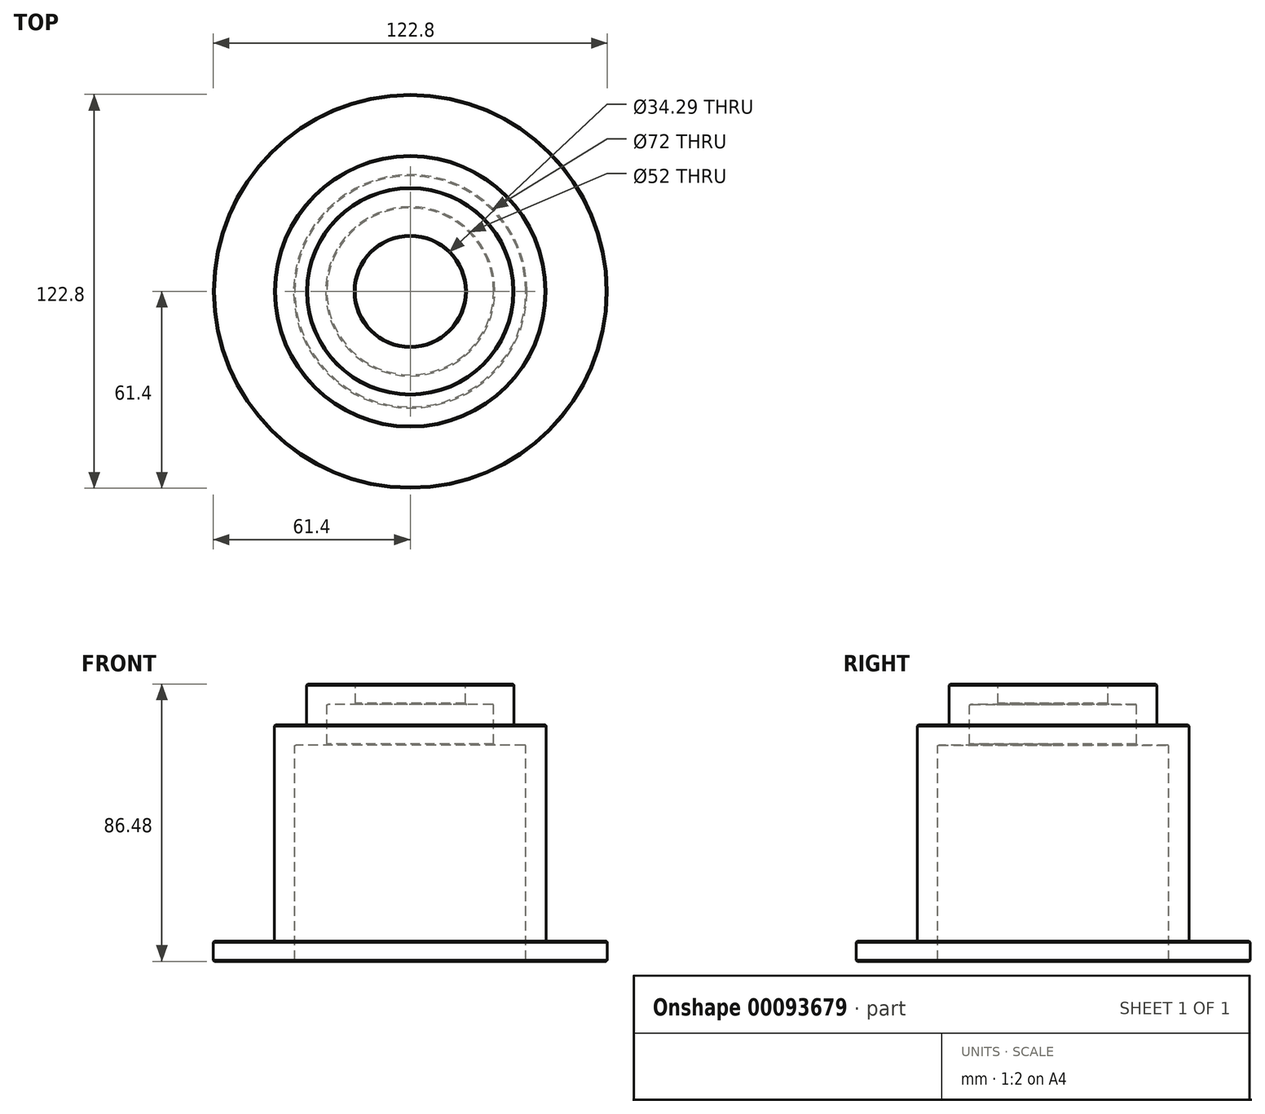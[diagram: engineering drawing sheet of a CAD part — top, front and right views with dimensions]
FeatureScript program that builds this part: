
annotation { "Feature Type Name" : "Feature", "Feature Type Description" : "" }
export const myFeature = defineFeature(function(context is Context, id is Id, definition is map)
    precondition{}
    {
        {
            var Q0;
            Q0=qCreatedBy(makeId("Front.planeOp"),FACE);
            var sketch = newSketch(context, id + "F0", { "sketchPlane" : qUnion([Q0])});
            skLineSegment(sketch, "E0", {"start": v(-17.15, 0) * mm, "end": v(-26, 0) * mm});
            skLineSegment(sketch, "E1", {"start": v(-26, 0) * mm, "end": v(-26, -12.7) * mm});
            skLineSegment(sketch, "E2", {"start": v(-26, -12.7) * mm, "end": v(-36, -12.7) * mm});
            skLineSegment(sketch, "E3", {"start": v(-36, -12.7) * mm, "end": v(-36, -80.13) * mm});
            skLineSegment(sketch, "E4", {"start": v(-36, -80.13) * mm, "end": v(-61.4, -80.13) * mm});
            skLineSegment(sketch, "E5.0", {"start": v(-42.35, -73.78) * mm, "end": v(-61.4, -73.78) * mm});
            skLineSegment(sketch, "E5.1", {"start": v(-17.15, 6.35) * mm, "end": v(-32.35, 6.35) * mm});
            skLineSegment(sketch, "E5.2", {"start": v(-32.35, 6.35) * mm, "end": v(-32.35, -6.35) * mm});
            skLineSegment(sketch, "E5.3", {"start": v(-32.35, -6.35) * mm, "end": v(-42.35, -6.35) * mm});
            skLineSegment(sketch, "E5.4", {"start": v(-42.35, -6.35) * mm, "end": v(-42.35, -73.78) * mm});
            skLineSegment(sketch, "E6", {"start": v(-17.15, 6.35) * mm, "end": v(-17.15, 0) * mm});
            skLineSegment(sketch, "E7", {"start": v(-61.4, -73.78) * mm, "end": v(-61.4, -80.13) * mm});
            skLineSegment(sketch, "E8", {"start": v(0, 32.3) * mm, "end": v(0, -87.06) * mm, "construction": true});
            skSolve(sketch);
        }
        {
            var Q0;
            Q0=qSketchRegion(id+"F0",true);
            var Q1;
            Q1=sQuery(id+"F0.wireOp",EDGE,"E8");
            revolve(context, id + "F1", {"entities" : qUnion([Q0]), "axis" : qUnion([Q1]), "revolveType" : RevolveType.FULL});
        }
        {
            var Q0;
            Q0=makeQuery(id+"F1.opRevolve","SWEPT_EDGE",EDGE,{"disambiguationData":[OSD([sQuery(id+"F0.wireOp",EDGE,"E5.2"),sQuery(id+"F0.wireOp",EDGE,"E5.3")])]});
            var Q1;
            Q1=makeQuery(id+"F1.opRevolve","SWEPT_EDGE",EDGE,{"disambiguationData":[OSD([sQuery(id+"F0.wireOp",EDGE,"E5.0"),sQuery(id+"F0.wireOp",EDGE,"E5.4")])]});
            var Q2;
            Q2=makeQuery(id+"F1.opRevolve","SWEPT_EDGE",EDGE,{"disambiguationData":[OSD([sQuery(id+"F0.wireOp",EDGE,"E2"),sQuery(id+"F0.wireOp",EDGE,"E3")])]});
            var Q3;
            Q3=makeQuery(id+"F1.opRevolve","SWEPT_EDGE",EDGE,{"disambiguationData":[OSD([sQuery(id+"F0.wireOp",EDGE,"E0"),sQuery(id+"F0.wireOp",EDGE,"E1")])]});
            fillet(context, id + "F2", {"entities" : qUnion([Q0, Q1, Q2, Q3]), "radius" : 0.38 * mm, "tangentPropagation" : true, "allowEdgeOverflow" : false});
        }
        {
            var Q0;
            Q0=makeQuery(id+"F1.opRevolve","SWEPT_EDGE",EDGE,{"disambiguationData":[OSD([sQuery(id+"F0.wireOp",EDGE,"E5.1"),sQuery(id+"F0.wireOp",EDGE,"E5.2")])]});
            var Q1;
            Q1=makeQuery(id+"F1.opRevolve","SWEPT_EDGE",EDGE,{"disambiguationData":[OSD([sQuery(id+"F0.wireOp",EDGE,"E5.1"),sQuery(id+"F0.wireOp",EDGE,"E6")])]});
            var Q2;
            Q2=makeQuery(id+"F1.opRevolve","SWEPT_EDGE",EDGE,{"disambiguationData":[OSD([sQuery(id+"F0.wireOp",EDGE,"E5.3"),sQuery(id+"F0.wireOp",EDGE,"E5.4")])]});
            var Q3;
            Q3=makeQuery(id+"F1.opRevolve","SWEPT_EDGE",EDGE,{"disambiguationData":[OSD([sQuery(id+"F0.wireOp",EDGE,"E5.0"),sQuery(id+"F0.wireOp",EDGE,"E7")])]});
            var Q4;
            Q4=makeQuery(id+"F1.opRevolve","SWEPT_EDGE",EDGE,{"disambiguationData":[OSD([sQuery(id+"F0.wireOp",EDGE,"E4"),sQuery(id+"F0.wireOp",EDGE,"E7")])]});
            var Q5;
            Q5=makeQuery(id+"F1.opRevolve","SWEPT_EDGE",EDGE,{"disambiguationData":[OSD([sQuery(id+"F0.wireOp",EDGE,"E3"),sQuery(id+"F0.wireOp",EDGE,"E4")])]});
            var Q6;
            Q6=makeQuery(id+"F1.opRevolve","SWEPT_EDGE",EDGE,{"disambiguationData":[OSD([sQuery(id+"F0.wireOp",EDGE,"E1"),sQuery(id+"F0.wireOp",EDGE,"E2")])]});
            var Q7;
            Q7=makeQuery(id+"F1.opRevolve","SWEPT_EDGE",EDGE,{"disambiguationData":[OSD([sQuery(id+"F0.wireOp",EDGE,"E0"),sQuery(id+"F0.wireOp",EDGE,"E6")])]});
            chamfer(context, id + "F3", {"entities" : qUnion([Q0, Q1, Q2, Q3, Q4, Q5, Q6, Q7]), "width" : 0.38 * mm, "tangentPropagation" : true});
        }
    });
